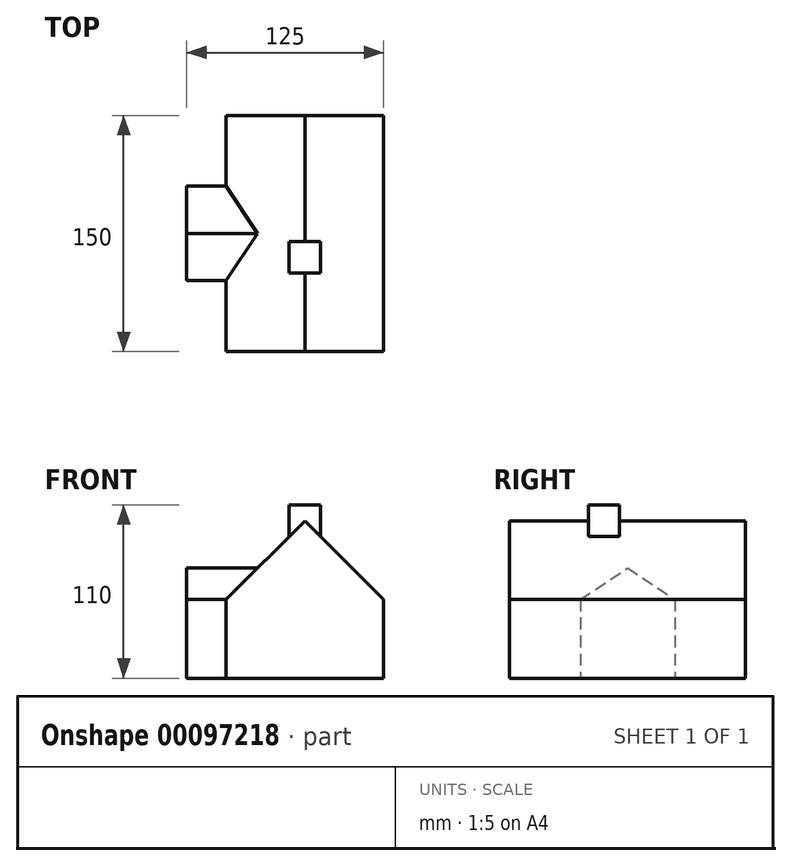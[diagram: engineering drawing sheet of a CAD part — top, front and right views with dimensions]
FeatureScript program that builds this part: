
annotation { "Feature Type Name" : "Feature", "Feature Type Description" : "" }
export const myFeature = defineFeature(function(context is Context, id is Id, definition is map)
    precondition{}
    {
        {
            var Q0;
            Q0=qCreatedBy(makeId("Front.planeOp"),FACE);
            var sketch = newSketch(context, id + "F0", { "sketchPlane" : qUnion([Q0])});
            skLineSegment(sketch, "E0.bottom", {"start": v(0, 0) * mm, "end": v(100, 0) * mm});
            skLineSegment(sketch, "E0.top", {"start": v(0, 50) * mm, "end": v(100, 50) * mm, "construction": true});
            skLineSegment(sketch, "E0.left", {"start": v(0, 0) * mm, "end": v(0, 50) * mm});
            skLineSegment(sketch, "E0.right", {"start": v(100, 0) * mm, "end": v(100, 50) * mm});
            skLineSegment(sketch, "E1", {"start": v(0, 50) * mm, "end": v(50, 100) * mm});
            skLineSegment(sketch, "E2", {"start": v(50, 100) * mm, "end": v(100, 50) * mm});
            skLineSegment(sketch, "E3", {"start": v(50, 50) * mm, "end": v(50, 100) * mm, "construction": true});
            skSolve(sketch);
        }
        {
            var Q0;
            Q0=makeQuery(id+"F0.imprint","IMPRINT",FACE,{"disambiguationData":[TD([[makeQuery(id+"F0.imprint","IMPRINT",EDGE,{"derivedFrom":sQuery(id+"F0.wireOp",EDGE,"E0.bottom")}),1.0]])]});
            extrude(context, id + "F1", {"entities" : qUnion([Q0]), "depth" : 150 * mm});
        }
        {
            var Q0;
            Q0=makeQuery(id+"F1.opExtrude","SWEPT_FACE",FACE,{"disambiguationData":[OSD([sQuery(id+"F0.wireOp",EDGE,"E0.left")])]});
            var sketch = newSketch(context, id + "F2", { "sketchPlane" : qUnion([Q0])});
            skLineSegment(sketch, "E4.bottom", {"start": v(45, 0) * mm, "end": v(105, 0) * mm});
            skLineSegment(sketch, "E4.top", {"start": v(45, 50) * mm, "end": v(105, 50) * mm, "construction": true});
            skLineSegment(sketch, "E4.left", {"start": v(45, 0) * mm, "end": v(45, 50) * mm});
            skLineSegment(sketch, "E4.right", {"start": v(105, 0) * mm, "end": v(105, 50) * mm});
            skLineSegment(sketch, "E5", {"start": v(45, 50) * mm, "end": v(75, 70) * mm});
            skLineSegment(sketch, "E6", {"start": v(75, 70) * mm, "end": v(105, 50) * mm});
            skLineSegment(sketch, "E7", {"start": v(75, 50) * mm, "end": v(75, 70) * mm, "construction": true});
            skLineSegment(sketch, "E8", {"start": v(75, 50) * mm, "end": v(75, 0) * mm, "construction": true});
            skSolve(sketch);
        }
        {
            var Q0;
            Q0 = qSketchRegion(id + "F2", true);
            extrude(context, id + "F3", {"entities" : qUnion([Q0]), "operationType" : NewBodyOperationType.ADD, "depth" : 25 * mm, "hasSecondDirection" : true, "secondDirectionOppositeDirection" : true, "secondDirectionDepth" : 25 * mm});
        }
        {
            var Q0;
            Q0=makeQuery(id+"F1.opExtrude","CAP_FACE",FACE,{"disambiguationData":[OSD([sQuery(id+"F0.wireOp",EDGE,"E0.bottom"),sQuery(id+"F0.wireOp",EDGE,"E0.left"),sQuery(id+"F0.wireOp",EDGE,"E0.right"),sQuery(id+"F0.wireOp",EDGE,"E1"),sQuery(id+"F0.wireOp",EDGE,"E2")])],"isStart":false});
            cPlane(context, id + "F4", {"entities" : qUnion([Q0]), "cplaneType" : CPlaneType.OFFSET, "offset" : 50 * mm, "oppositeDirection" : true, "width" : 150 * mm, "height" : 150 * mm});
        }
        {
            var Q0;
            Q0=qCreatedBy(id+"F4.planeOp",FACE);
            var sketch = newSketch(context, id + "F5", { "sketchPlane" : qUnion([Q0])});
            skLineSegment(sketch, "E9.bottom", {"start": v(40, 90) * mm, "end": v(60, 90) * mm});
            skLineSegment(sketch, "E9.top", {"start": v(40, 110) * mm, "end": v(60, 110) * mm});
            skLineSegment(sketch, "E9.left", {"start": v(40, 90) * mm, "end": v(40, 110) * mm});
            skLineSegment(sketch, "E9.right", {"start": v(60, 90) * mm, "end": v(60, 110) * mm});
            skSolve(sketch);
        }
        {
            var Q0;
            Q0=makeQuery(id+"F5.imprint","IMPRINT",FACE,{"disambiguationData":[TD([[makeQuery(id+"F5.imprint","IMPRINT",EDGE,{"derivedFrom":sQuery(id+"F5.wireOp",EDGE,"E9.bottom")}),1.0]])]});
            extrude(context, id + "F6", {"entities" : qUnion([Q0]), "operationType" : NewBodyOperationType.ADD, "oppositeDirection" : true, "depth" : 20 * mm});
        }
    });
